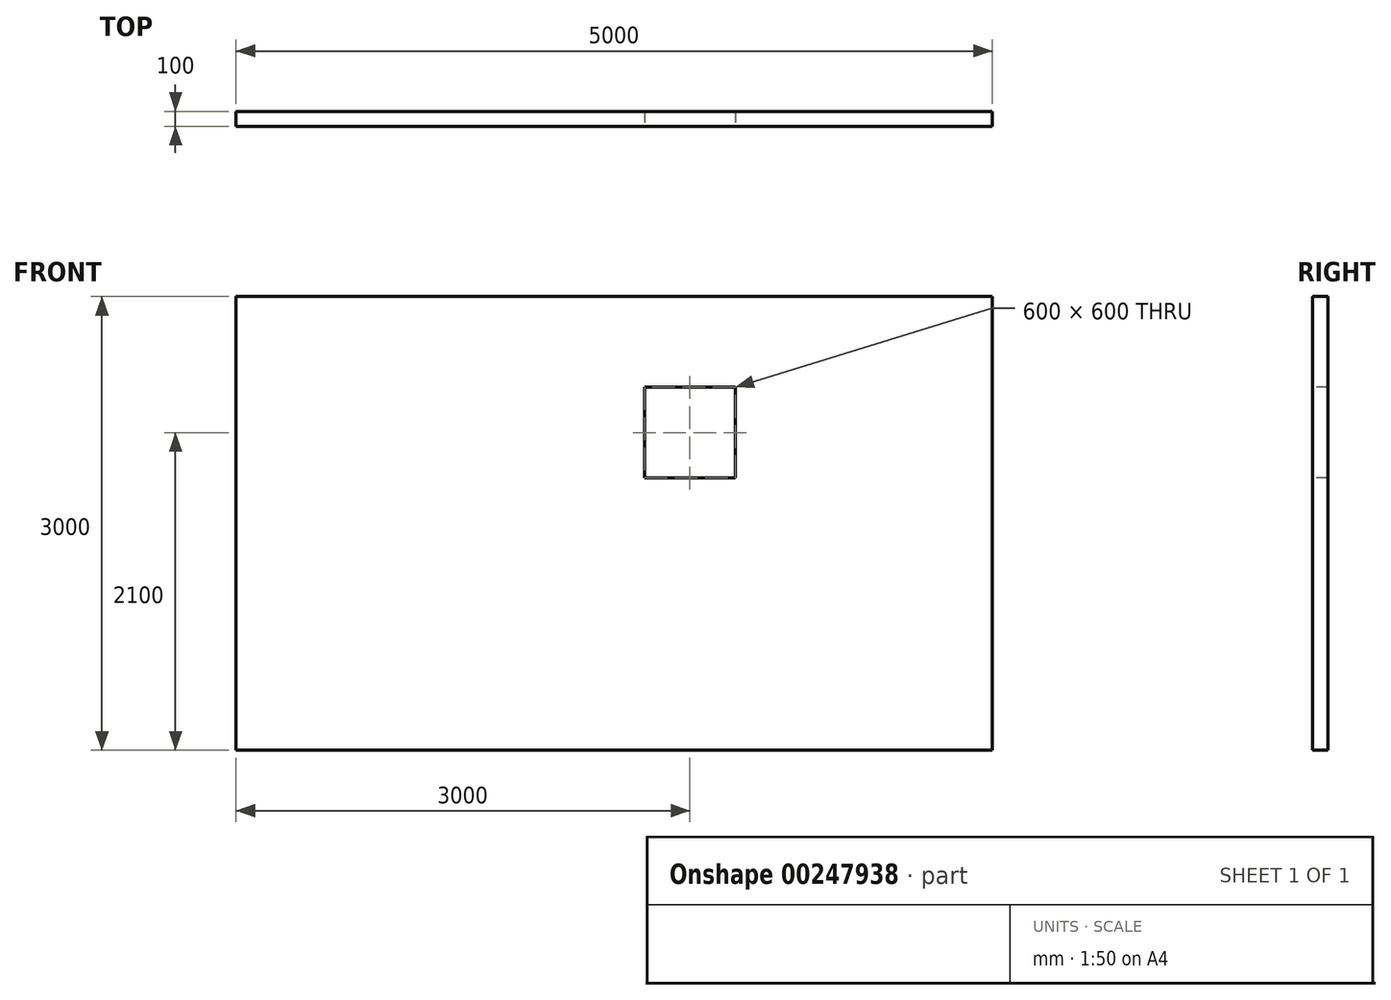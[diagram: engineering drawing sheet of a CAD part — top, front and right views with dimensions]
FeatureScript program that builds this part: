
annotation { "Feature Type Name" : "Feature", "Feature Type Description" : "" }
export const myFeature = defineFeature(function(context is Context, id is Id, definition is map)
    precondition{}
    {
        {
            var Q0;
            Q0=qCreatedBy(makeId("Front.planeOp"),FACE);
            var sketch = newSketch(context, id + "F0", { "sketchPlane" : qUnion([Q0])});
            skLineSegment(sketch, "E0.bottom", {"start": v(2500, 0) * mm, "end": v(-2500, 0) * mm});
            skLineSegment(sketch, "E0.top", {"start": v(2500, 3000) * mm, "end": v(-2500, 3000) * mm});
            skLineSegment(sketch, "E0.left", {"start": v(2500, 0) * mm, "end": v(2500, 3000) * mm});
            skLineSegment(sketch, "E0.right", {"start": v(-2500, 0) * mm, "end": v(-2500, 3000) * mm});
            skPoint(sketch, "E0.middle", {"position": v(0, 1500) * mm});
            skSolve(sketch);
        }
        {
            var Q0;
            Q0=makeQuery(id+"F0.imprint","IMPRINT",FACE,{"disambiguationData":[TD([[makeQuery(id+"F0.imprint","IMPRINT",EDGE,{"derivedFrom":sQuery(id+"F0.wireOp",EDGE,"E0.bottom")}),-1.0]])]});
            extrude(context, id + "F1", {"entities" : qUnion([Q0]), "endBound" : BoundingType.SYMMETRIC, "depth" : 100 * mm});
        }
        {
            var Q0;
            Q0=makeQuery(id+"F1.opExtrude","CAP_FACE",FACE,{"disambiguationData":[OSD([sQuery(id+"F0.wireOp",EDGE,"E0.bottom"),sQuery(id+"F0.wireOp",EDGE,"E0.top"),sQuery(id+"F0.wireOp",EDGE,"E0.left"),sQuery(id+"F0.wireOp",EDGE,"E0.right")])],"isStart":false});
            var sketch = newSketch(context, id + "F2", { "sketchPlane" : qUnion([Q0])});
            skLineSegment(sketch, "E1", {"start": v(0, 0) * mm, "end": v(0, 3000) * mm, "construction": true});
            skLineSegment(sketch, "E2", {"start": v(1000, 3000) * mm, "end": v(1000, 0) * mm, "construction": true});
            skLineSegment(sketch, "E3", {"start": v(0, 3000) * mm, "end": v(1000, 3000) * mm, "construction": true});
            skLineSegment(sketch, "E4.bottom", {"start": v(800, 1800) * mm, "end": v(200, 1800) * mm});
            skLineSegment(sketch, "E4.top", {"start": v(800, 2400) * mm, "end": v(200, 2400) * mm});
            skLineSegment(sketch, "E4.left", {"start": v(800, 1800) * mm, "end": v(800, 2400) * mm});
            skLineSegment(sketch, "E4.right", {"start": v(200, 1800) * mm, "end": v(200, 2400) * mm});
            skPoint(sketch, "E4.middle", {"position": v(500, 2100) * mm});
            skPoint(sketch, "E5", {"position": v(500, 3000) * mm});
            skSolve(sketch);
        }
        {
            var Q0;
            Q0=makeQuery(id+"F2.imprint","IMPRINT",FACE,{"disambiguationData":[TD([[makeQuery(id+"F2.imprint","IMPRINT",EDGE,{"derivedFrom":sQuery(id+"F2.wireOp",EDGE,"E4.bottom")}),-1.0]])]});
            extrude(context, id + "F3", {"entities" : qUnion([Q0]), "operationType" : NewBodyOperationType.REMOVE, "endBound" : BoundingType.THROUGH_ALL, "oppositeDirection" : true, "depth" : 25 * mm});
        }
    });
